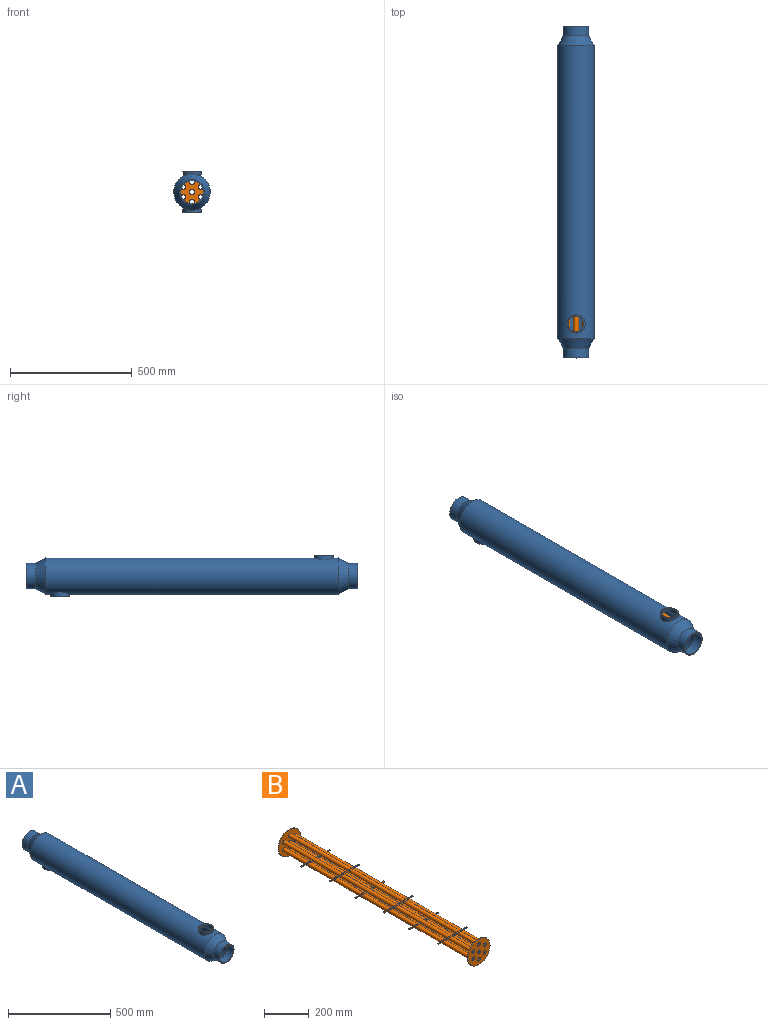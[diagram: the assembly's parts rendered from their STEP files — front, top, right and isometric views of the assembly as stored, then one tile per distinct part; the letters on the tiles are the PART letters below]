
ASSEMBLY  parts=2 mates=2
PART A: 18 faces, bbox 150x1365x170 mm
  f0: cylinder r=75mm len=1205mm, axis (0,-1,0), area 558717mm2, adj f2,f3,f14,f17
  f1: cylinder r=70mm len=1205mm, axis (0,-1,0), area 523166.6mm2, adj f7,f8,f12,f15
  f2: cone r=51.8mm half-angle=30.1deg, axis (0,-1,0), area 18420.3mm2, adj f0,f11
  f3: cone r=51.8mm half-angle=30.1deg, axis (0,1,0), area 18420.3mm2, adj f0,f4
  f4: cylinder r=51.8mm len=103.6mm, axis (0,-1,0), area 13018.8mm2, adj f3,f5
  f5: plane 103.6x103.6mm, normal (0,-1,0), area 1548.8mm2, adj f4,f6
  f6: cylinder r=46.8mm len=93.6mm, axis (0,-1,0), area 11762.2mm2, adj f5,f7
  f7: cone r=70mm half-angle=30.1deg, axis (0,1,0), area 16967.6mm2, adj f1,f6
  f8: cone r=70mm half-angle=30.1deg, axis (0,-1,0), area 16967.6mm2, adj f1,f9
  f9: cylinder r=46.8mm len=93.6mm, axis (0,-1,0), area 11762.2mm2, adj f8,f10
  f10: plane 103.6x103.6mm, normal (0,1,0), area 1548.8mm2, adj f9,f11
  f11: cylinder r=51.8mm len=103.6mm, axis (0,-1,0), area 13018.8mm2, adj f2,f10
  f12: cylinder r=32.5mm len=65mm, axis (0,0,1), area 3866.5mm2, adj f1,f16
  f13: plane 75x75mm, normal (0,0,-1), area 1099.6mm2, adj f14,f15
  f14: cylinder r=37.5mm len=75mm, axis (0,0,-1), area 3518.8mm2, adj f0,f13
  f15: cylinder r=32.5mm len=65mm, axis (0,0,-1), area 3867.9mm2, adj f1,f13
  f16: plane 75x75mm, normal (0,0,1), area 1099.6mm2, adj f12,f17
  f17: cylinder r=37.5mm len=75mm, axis (0,0,1), area 3518.1mm2, adj f0,f16
PART B: 86 faces, bbox 144.6x1209.6x144.6 mm
  f0: plane 140x140mm, normal (0,1,0), area 13409.1mm2, adj f1,f79,f80,f81,f82,f83,f84,f85
  f1: cylinder r=9.5mm len=1205mm, axis (0,-1,0), area 71926.8mm2, adj f0,f2
  f2: plane 140x140mm, normal (0,-1,0), area 13409.1mm2, adj f1,f3,f79,f80,f81,f82,f83,f84
  f3: cylinder r=70mm len=140mm, axis (0,1,0), area 2199.1mm2, adj f2,f4
  f4: plane 140x140mm, normal (0,1,0), area 12969.3mm2, adj f3,f5,f73,f74,f75,f76,f77,f78
  f5: cylinder r=10.5mm len=367.81mm, axis (0,-1,0), area 23332.9mm2, adj f4,f6,f10,f11,f12,f72
  f6: plane 20.78x7.07mm, normal (0,0,-1), area 146.9mm2, adj f5,f7,f10,f12
  f7: cylinder r=70mm len=140mm, axis (0,1,0), area 1809.4mm2, adj f6,f8,f9,f10,f12
  f8: plane 20.78x7.07mm, normal (0,0,-1), area 146.9mm2, adj f7,f10,f12,f77
  f9: cylinder r=100mm len=33.85mm, axis (0,0.71,0.71), area 0mm2, adj f7,f10
  f10: plane 144.42x94.36mm, normal (0,-0.71,-0.71), area 12466.9mm2, adj f5,f6,f7,f8,f9,f11,f73,f74
  f11: plane 50.04x7.07mm, normal (0,0,-1), area 353.8mm2, adj f5,f10,f12,f77
  f12: plane 140x91mm, normal (0,0.71,0.71), area 12500.8mm2, adj f5,f6,f7,f8,f11,f13,f69,f70
  f13: cylinder r=10.5mm len=356.94mm, axis (0,-1,0), area 21912.8mm2, adj f12,f14,f66,f67,f68,f72
  f14: plane 140x89.94mm, normal (0,0.71,0.71), area 12466.9mm2, adj f13,f15,f16,f17,f18,f63,f64,f65
  f15: cylinder r=100mm len=33.85mm, axis (0,0.71,0.71), area 0mm2, adj f14,f16
  f16: cylinder r=70mm len=140mm, axis (0,1,0), area 1809.4mm2, adj f14,f15,f17,f67,f72
  f17: plane 20.78x7.07mm, normal (0,0,1), area 146.9mm2, adj f14,f16,f71,f72
  f18: cylinder r=10.5mm len=356.94mm, axis (0,-1,0), area 21912.8mm2, adj f14,f19,f20,f24,f62,f68
  f19: plane 50.04x7.07mm, normal (0,0,-1), area 353.8mm2, adj f18,f24,f64,f68
  f20: plane 20.78x7.07mm, normal (0,0,-1), area 146.9mm2, adj f18,f21,f24,f68
  f21: cylinder r=70mm len=140mm, axis (0,1,0), area 1809.4mm2, adj f20,f22,f23,f24,f68
  f22: cylinder r=100mm len=33.85mm, axis (0,0.71,0.71), area 0mm2, adj f21,f68
  f23: plane 20.78x7.07mm, normal (0,0,-1), area 146.9mm2, adj f21,f24,f64,f68
  f24: plane 144.57x95.57mm, normal (0,0.71,0.71), area 12500.8mm2, adj f18,f19,f20,f21,f23,f25,f26,f60
  f25: cylinder r=10.5mm len=185.51mm, axis (0,-1,0), area 10843.3mm2, adj f24,f62
  f26: cylinder r=10.5mm len=356.94mm, axis (0,-1,0), area 21912.8mm2, adj f24,f27,f57,f58,f59,f62
  f27: plane 140x89.94mm, normal (0,0.71,0.71), area 12466.9mm2, adj f26,f28,f29,f30,f31,f32,f55,f56
  f28: cylinder r=100mm len=33.85mm, axis (0,0.71,0.71), area 0mm2, adj f27,f29
  f29: cylinder r=70mm len=140mm, axis (0,1,0), area 1809.4mm2, adj f27,f28,f30,f58,f62
  f30: plane 20.78x7.07mm, normal (0,0,1), area 146.9mm2, adj f27,f29,f61,f62
  f31: cylinder r=10.5mm len=185.51mm, axis (0,-1,0), area 10843.3mm2, adj f27,f59
  f32: cylinder r=10.5mm len=356.94mm, axis (0,-1,0), area 21912.8mm2, adj f27,f33,f34,f38,f54,f59
  f33: plane 50.04x7.07mm, normal (0,0,-1), area 353.8mm2, adj f32,f38,f55,f59
  f34: plane 20.78x7.07mm, normal (0,0,-1), area 146.9mm2, adj f32,f35,f38,f59
  f35: cylinder r=70mm len=140mm, axis (0,1,0), area 1809.4mm2, adj f34,f36,f37,f38,f59
  f36: cylinder r=100mm len=33.85mm, axis (0,0.71,0.71), area 0mm2, adj f35,f59
  f37: plane 20.78x7.07mm, normal (0,0,-1), area 146.9mm2, adj f35,f38,f55,f59
  f38: plane 144.57x95.57mm, normal (0,0.71,0.71), area 12500.8mm2, adj f32,f33,f34,f35,f37,f39,f40,f52
  f39: cylinder r=10.5mm len=185.51mm, axis (0,-1,0), area 10843.3mm2, adj f38,f54
  f40: cylinder r=10.5mm len=367.82mm, axis (0,-1,0), area 23333.6mm2, adj f38,f41,f42,f46,f51,f54
  f41: plane 50.04x7.07mm, normal (0,0,1), area 353.8mm2, adj f40,f46,f53,f54
  f42: plane 20.78x7.07mm, normal (0,0,1), area 146.9mm2, adj f40,f43,f46,f54
  f43: cylinder r=70mm len=140mm, axis (0,1,0), area 1809.4mm2, adj f42,f44,f45,f46,f54
  f44: plane 20.78x7.07mm, normal (0,0,1), area 146.9mm2, adj f43,f46,f53,f54
  f45: cylinder r=100mm len=33.85mm, axis (0,0.71,0.71), area 0mm2, adj f43,f46
  f46: plane 144.57x94.51mm, normal (0,0.71,0.71), area 12466.9mm2, adj f40,f41,f42,f43,f44,f45,f47,f48
  f47: cylinder r=10.5mm len=175.89mm, axis (0,-1,0), area 10911.6mm2, adj f46,f51
  f48: cylinder r=10.5mm len=155.39mm, axis (0,-1,0), area 9559.2mm2, adj f46,f51
  f49: cylinder r=10.5mm len=155.39mm, axis (0,-1,0), area 9559.2mm2, adj f46,f51
  f50: cylinder r=10.5mm len=134.89mm, axis (0,-1,0), area 8206.7mm2, adj f46,f51
  f51: plane 140x140mm, normal (0,-1,0), area 12969.3mm2, adj f40,f47,f48,f49,f50,f52,f53,f85
  f52: cylinder r=10.5mm len=388.32mm, axis (0,-1,0), area 24926.4mm2, adj f38,f51
  f53: cylinder r=10.5mm len=367.82mm, axis (0,-1,0), area 23333.6mm2, adj f38,f41,f44,f46,f51,f54
  f54: plane 144.57x95.57mm, normal (0,-0.71,-0.71), area 12500.8mm2, adj f32,f39,f40,f41,f42,f43,f44,f53
  f55: cylinder r=10.5mm len=356.94mm, axis (0,-1,0), area 21912.8mm2, adj f27,f33,f37,f38,f54,f59
  f56: cylinder r=10.5mm len=356.94mm, axis (0,-1,0), area 22153.2mm2, adj f27,f54
  f57: plane 50.04x7.07mm, normal (0,0,1), area 353.8mm2, adj f26,f27,f61,f62
  f58: plane 20.78x7.07mm, normal (0,0,1), area 146.9mm2, adj f26,f27,f29,f62
  f59: plane 144.57x94.51mm, normal (0,-0.71,-0.71), area 12466.9mm2, adj f26,f31,f32,f33,f34,f35,f36,f37
  f60: cylinder r=10.5mm len=356.94mm, axis (0,-1,0), area 22153.2mm2, adj f24,f59
  f61: cylinder r=10.5mm len=356.94mm, axis (0,-1,0), area 21912.8mm2, adj f24,f27,f30,f57,f59,f62
  f62: plane 140x91mm, normal (0,-0.71,-0.71), area 12500.8mm2, adj f18,f25,f26,f29,f30,f57,f58,f61
  f63: cylinder r=10.5mm len=185.51mm, axis (0,-1,0), area 10843.3mm2, adj f14,f68
  f64: cylinder r=10.5mm len=356.94mm, axis (0,-1,0), area 21912.8mm2, adj f14,f19,f23,f24,f62,f68
  f65: cylinder r=10.5mm len=356.94mm, axis (0,-1,0), area 22153.2mm2, adj f14,f62
  f66: plane 50.04x7.07mm, normal (0,0,1), area 353.8mm2, adj f13,f14,f71,f72
  f67: plane 20.78x7.07mm, normal (0,0,1), area 146.9mm2, adj f13,f14,f16,f72
  f68: plane 144.57x94.51mm, normal (0,-0.71,-0.71), area 12466.9mm2, adj f13,f18,f19,f20,f21,f22,f23,f63
  f69: cylinder r=10.5mm len=185.51mm, axis (0,-1,0), area 10843.3mm2, adj f12,f72
  f70: cylinder r=10.5mm len=356.94mm, axis (0,-1,0), area 22153.2mm2, adj f12,f68
  f71: cylinder r=10.5mm len=356.94mm, axis (0,-1,0), area 21912.8mm2, adj f12,f14,f17,f66,f68,f72
  f72: plane 144.42x95.42mm, normal (0,-0.71,-0.71), area 12500.8mm2, adj f5,f13,f16,f17,f66,f67,f69,f71
  f73: cylinder r=10.5mm len=155.38mm, axis (0,-1,0), area 9558.5mm2, adj f4,f10
  f74: cylinder r=10.5mm len=175.88mm, axis (0,-1,0), area 10911mm2, adj f4,f10
  f75: cylinder r=10.5mm len=134.88mm, axis (0,-1,0), area 8206.1mm2, adj f4,f10
  f76: cylinder r=10.5mm len=155.38mm, axis (0,-1,0), area 9558.5mm2, adj f4,f10
  f77: cylinder r=10.5mm len=367.81mm, axis (0,-1,0), area 23332.9mm2, adj f4,f8,f10,f11,f12,f72
  f78: cylinder r=10.5mm len=388.31mm, axis (0,-1,0), area 24925.7mm2, adj f4,f72
  f79: cylinder r=9.5mm len=1205mm, axis (0,-1,0), area 71926.8mm2, adj f0,f2
  f80: cylinder r=9.5mm len=1205mm, axis (0,-1,0), area 71926.8mm2, adj f0,f2
  f81: cylinder r=9.5mm len=1205mm, axis (0,-1,0), area 71926.8mm2, adj f0,f2
  f82: cylinder r=9.5mm len=1205mm, axis (0,-1,0), area 71926.8mm2, adj f0,f2
  f83: cylinder r=9.5mm len=1205mm, axis (0,-1,0), area 71926.8mm2, adj f0,f2
  f84: cylinder r=9.5mm len=1205mm, axis (0,-1,0), area 71926.8mm2, adj f0,f2
  f85: cylinder r=70mm len=140mm, axis (0,1,0), area 2199.1mm2, adj f0,f51
PLACE A t=(-400.1,-517.39,-429.58)mm
PLACE B t=(-400.1,82.61,-429.58)mm
MATE fastened A.f0 <-> B.f3  axis (0,-1,0) through (-400.1,-1119.89,-429.58)mm
MATE cylindrical A.f0 <-> B.f3  axis (0,-1,0) through (-400.1,-517.39,-429.58)mm
